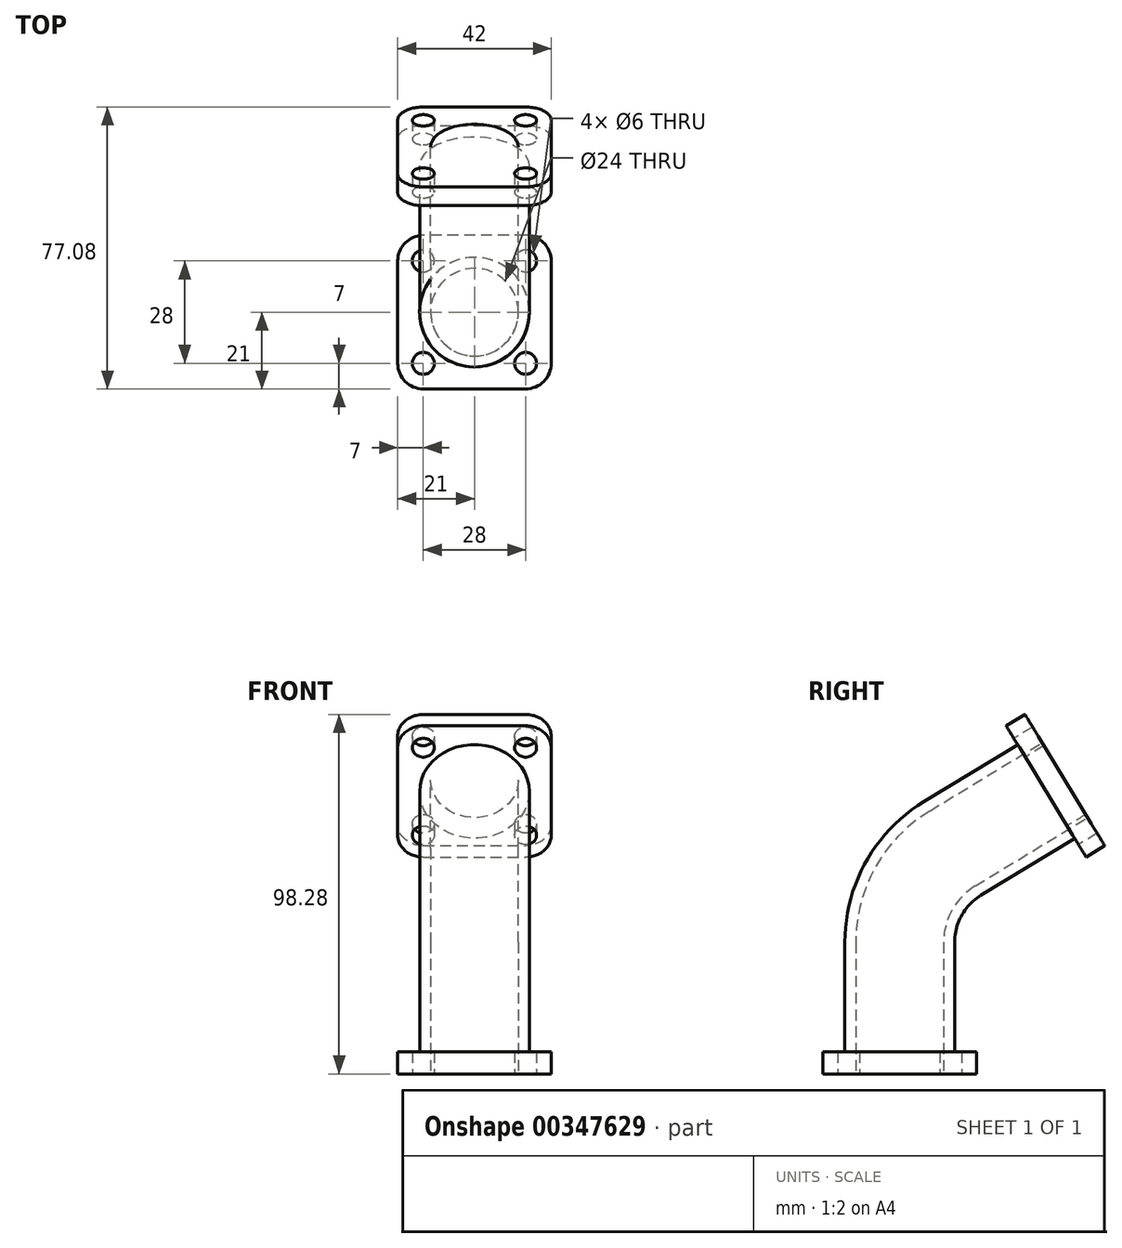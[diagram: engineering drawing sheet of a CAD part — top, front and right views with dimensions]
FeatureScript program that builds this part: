
annotation { "Feature Type Name" : "Feature", "Feature Type Description" : "" }
export const myFeature = defineFeature(function(context is Context, id is Id, definition is map)
    precondition{}
    {
        {
            var Q0;
            Q0=qCreatedBy(makeId("Top.planeOp"),FACE);
            var sketch = newSketch(context, id + "F0", { "sketchPlane" : qUnion([Q0])});
            skLineSegment(sketch, "E0.bottom", {"start": v(14, -21) * mm, "end": v(-14, -21) * mm});
            skLineSegment(sketch, "E0.top", {"start": v(14, 21) * mm, "end": v(-14, 21) * mm});
            skLineSegment(sketch, "E0.left", {"start": v(21, -14) * mm, "end": v(21, 14) * mm});
            skLineSegment(sketch, "E0.right", {"start": v(-21, -14) * mm, "end": v(-21, 14) * mm});
            skPoint(sketch, "E0.middle", {"position": v(0, 0) * mm});
            skPoint(sketch, "E1.visualSharp", {"position": v(-21, 21) * mm});
            skArc(sketch, "E1.filletArc", {"start": v(-14, 21) * mm, "mid": v(-18.95, 18.95) * mm, "end": v(-21, 14) * mm});
            skPoint(sketch, "E2.visualSharp", {"position": v(21, 21) * mm});
            skArc(sketch, "E2.filletArc", {"start": v(21, 14) * mm, "mid": v(18.95, 18.95) * mm, "end": v(14, 21) * mm});
            skPoint(sketch, "E3.visualSharp", {"position": v(21, -21) * mm});
            skArc(sketch, "E3.filletArc", {"start": v(14, -21) * mm, "mid": v(18.95, -18.95) * mm, "end": v(21, -14) * mm});
            skPoint(sketch, "E4.visualSharp", {"position": v(-21, -21) * mm});
            skArc(sketch, "E4.filletArc", {"start": v(-21, -14) * mm, "mid": v(-18.95, -18.95) * mm, "end": v(-14, -21) * mm});
            skCircle(sketch, "E5", {"center": v(-14, 14) * mm, "radius": 3 * mm});
            skCircle(sketch, "E6", {"center": v(14, 14) * mm, "radius": 3 * mm});
            skCircle(sketch, "E7", {"center": v(-14, -14) * mm, "radius": 3 * mm});
            skCircle(sketch, "E8", {"center": v(14, -14) * mm, "radius": 3 * mm});
            skCircle(sketch, "E9", {"center": v(0, 0) * mm, "radius": 12 * mm});
            skSolve(sketch);
        }
        {
            var Q0;
            Q0=makeQuery(id+"F0.imprint","IMPRINT",FACE,{"disambiguationData":[TD([[makeQuery(id+"F0.imprint","IMPRINT",EDGE,{"derivedFrom":sQuery(id+"F0.wireOp",EDGE,"E0.bottom")}),-1.0]])]});
            extrude(context, id + "F1", {"entities" : qUnion([Q0]), "depth" : 6 * mm});
        }
        {
            var Q0;
            Q0=makeQuery(id+"F1.opExtrude","CAP_FACE",FACE,{"disambiguationData":[OSD([sQuery(id+"F0.wireOp",EDGE,"E0.bottom"),sQuery(id+"F0.wireOp",EDGE,"E0.top"),sQuery(id+"F0.wireOp",EDGE,"E0.left"),sQuery(id+"F0.wireOp",EDGE,"E0.right"),sQuery(id+"F0.wireOp",EDGE,"E1.filletArc"),sQuery(id+"F0.wireOp",EDGE,"E2.filletArc"),sQuery(id+"F0.wireOp",EDGE,"E3.filletArc"),sQuery(id+"F0.wireOp",EDGE,"E4.filletArc"),sQuery(id+"F0.wireOp",EDGE,"E5"),sQuery(id+"F0.wireOp",EDGE,"E6"),sQuery(id+"F0.wireOp",EDGE,"E7"),sQuery(id+"F0.wireOp",EDGE,"E8"),sQuery(id+"F0.wireOp",EDGE,"E9")])],"isStart":false});
            var sketch = newSketch(context, id + "F2", { "sketchPlane" : qUnion([Q0])});
            skCircle(sketch, "E10", {"center": v(0, 0) * mm, "radius": 12 * mm});
            skCircle(sketch, "E11", {"center": v(0, 0) * mm, "radius": 15 * mm});
            skSolve(sketch);
        }
        {
            var Q0;
            Q0=qCreatedBy(makeId("Right.planeOp"),FACE);
            var sketch = newSketch(context, id + "F3", { "sketchPlane" : qUnion([Q0])});
            skArc(sketch, "E12", {"start": v(0, 36) * mm, "mid": v(3.85, 50.7) * mm, "end": v(14.41, 61.63) * mm});
            skLineSegment(sketch, "E13", {"start": v(14.41, 61.63) * mm, "end": v(40.05, 77.22) * mm});
            skLineSegment(sketch, "E14", {"start": v(0, 36) * mm, "end": v(0, 6) * mm});
            skSolve(sketch);
        }
        {
            var Q0;
            Q0=makeQuery(id+"F2.imprint","IMPRINT",FACE,{"disambiguationData":[TD([[makeQuery(id+"F2.imprint","IMPRINT",EDGE,{"derivedFrom":sQuery(id+"F2.wireOp",EDGE,"E10")}),-1.0]])]});
            var Q1;
            Q1=sQuery(id+"F3.wireOp",EDGE,"E14");
            var Q2;
            Q2=sQuery(id+"F3.wireOp",EDGE,"E12");
            var Q3;
            Q3=sQuery(id+"F3.wireOp",EDGE,"E13");
            sweep(context, id + "F4", {"operationType" : NewBodyOperationType.ADD, "profiles" : qUnion([Q0]), "path" : qUnion([Q1, Q2, Q3])});
        }
        {
            var Q0;
            Q0=makeQuery(id+"F4.opSweep","CAP_FACE",FACE,{"disambiguationData":[OSD([sQuery(id+"F2.wireOp",EDGE,"E10"),sQuery(id+"F2.wireOp",EDGE,"E11"),sQuery(id+"F3.wireOp",VERTEX,"E13.end")])],"isStart":false});
            var sketch = newSketch(context, id + "F5", { "sketchPlane" : qUnion([Q0])});
            skLineSegment(sketch, "E15.bottom", {"start": v(14, 24.17) * mm, "end": v(-14, 24.17) * mm});
            skLineSegment(sketch, "E15.top", {"start": v(14, 66.17) * mm, "end": v(-14, 66.17) * mm});
            skLineSegment(sketch, "E15.left", {"start": v(21, 31.17) * mm, "end": v(21, 59.17) * mm});
            skLineSegment(sketch, "E15.right", {"start": v(-21, 31.17) * mm, "end": v(-21, 59.17) * mm});
            skPoint(sketch, "E15.middle", {"position": v(0, 45.17) * mm});
            skPoint(sketch, "E16.visualSharp", {"position": v(-21, 66.17) * mm});
            skArc(sketch, "E16.filletArc", {"start": v(-14, 66.17) * mm, "mid": v(-18.95, 64.12) * mm, "end": v(-21, 59.17) * mm});
            skPoint(sketch, "E17.visualSharp", {"position": v(21, 66.17) * mm});
            skArc(sketch, "E17.filletArc", {"start": v(21, 59.17) * mm, "mid": v(18.95, 64.12) * mm, "end": v(14, 66.17) * mm});
            skPoint(sketch, "E18.visualSharp", {"position": v(21, 24.17) * mm});
            skArc(sketch, "E18.filletArc", {"start": v(14, 24.17) * mm, "mid": v(18.95, 26.22) * mm, "end": v(21, 31.17) * mm});
            skPoint(sketch, "E19.visualSharp", {"position": v(-21, 24.17) * mm});
            skArc(sketch, "E19.filletArc", {"start": v(-21, 31.17) * mm, "mid": v(-18.95, 26.22) * mm, "end": v(-14, 24.17) * mm});
            skCircle(sketch, "E20", {"center": v(-14, 59.17) * mm, "radius": 3 * mm});
            skCircle(sketch, "E21", {"center": v(14, 59.17) * mm, "radius": 3 * mm});
            skCircle(sketch, "E22", {"center": v(-14, 31.17) * mm, "radius": 3 * mm});
            skCircle(sketch, "E23", {"center": v(14, 31.17) * mm, "radius": 3 * mm});
            skCircle(sketch, "E24", {"center": v(0, 45.17) * mm, "radius": 12 * mm});
            skSolve(sketch);
        }
        {
            var Q0;
            Q0 = qSketchRegion(id + "F5", true);
            extrude(context, id + "F6", {"entities" : qUnion([Q0]), "operationType" : NewBodyOperationType.ADD, "depth" : 6 * mm});
        }
    });
